# Revit family: PRD_AR_WtrSpplFttngsFrWshBsnsAndTrghs_BasicInstallationKitForTap_F3BX1001,F5BX1001
name_source: partatom
category: Plumbing Fixtures
revit_build: Autodesk Revit 2018 (Build: 20190510_1515(x64)
units: mm (PartAtom-declared; Revit-internal decimal feet)

## family parameters
Cut with Voids When Loaded = Yes
Host = Face
OmniClass Number = 23.45.05.14.99
OmniClass Title = Other Sanitary Washing Plumbing Fixtures
Part Type = Normal
Room Calculation Point = No
Round Connector Dimension = Use Diameter
Shared = No

## types (2) — shared parameters
Application = washing
AssetType = Fixed
BarrierFree = no
Category = Pr_40_20_87_96, Washbasin manual water supply sets
CloseOffRating = 0.0 Pa
Default Elevation = 850 mm  [stored 2.78871 ft]
DiameterNominal = 15.000 mm
DurationUnit = year
Features = For connection to hot and cold water, 174 x 225 mm
Finish = synthetic
FlowCoefficient = 0
FlowColdWater = 0.0 L/s
FlowHotWater = 0.0 L/s
IfcExportAs = IfcValveType
IfcExportType = MIXING
Manufacturer = KWC Group AG
ManufacturerName = KWC Group AG
ManufacturerURL = www.kwc.com
Material = Plastic
MaterialsBody = Brass
MixerControl = Other
NBSDescription = Water supply fittings for wash basins and troughs
NBSReference = 45-35-70/371
OutletConnectionSize = 20 mm  [stored 0.0656168 ft]
PositionOfPowerConnection = from top
ProductInformation = https://pim.kwc.com
Size = 174 x 225
TestPressure = 0.0 Pa
TypeOfMixing = with thermostat / mixer
TypeOfMounting = in-wall installation with box
URL = www.kwc.com
Uniclass2015Code = Pr_40_20_87_96
Uniclass2015Title = Washbasin manual water supply sets
Uniclass2015Version = Products v1.10
ValveMaterial = PRD_AR_PlasticRed
ValveMechanism = Other
ValveOperation = Other
ValvePattern = STRAIGHT_3_PORT
Version = 1
WarrantyDurationUnit = year
zero-valued in all types: NominalHeight, NominalLength, NominalWidth

## per-type parameters (varying)
| type | BIMObjectName | Description | GrossWeight | Model | ModelNumber | ModelReference | Name | NetWeight | Type |
| F3BX1001 | PRD_AR_WaterSupplyFittingsForWashBasinsAndTroughs_BasicInstallationKitForTap_F3BX1001 | R3 basic installation kit for in-wall mounting of finished installation kits DN 15 with mixing unit, for sanitary facilities. For connection to hot and cold water. KWC system box made of plastic, 174 x 225 mm, with connection screws, shell protection, flush connector for flushing, and leak test. | 1.10 kg | F3BX1001 | 2030040479 | F3BX1001 | F3 basic installation kit for tap F3BX1001 | 1.00 kg | for built-in with box |
| F5BX1001 with sliding adhesive flange | PRD_AR_WaterSupplyFittingsForWashBasinsAndTroughs_BasicInstallationKitForTap_F5BX1001 | R5 basic installation kit with sliding adhesive flange for in-wall mounting of finished installation kits DN 15 with mixing unit, for sanitary facilities. For connection to hot and cold water. KWC system box made of plastic, 174 x 225 mm, with lockable connection screws, shell protection, flush connector for flushing, and leak test. Continuously-adjustable sliding adhesive flange with form-closed, flexible, 70 mm wide sealing collar. Sealing collar made of water-tight, permanently-elastic, alkali-resistant, and crack-bridging thermoplastic elastomer with polypropylene fleece for connecting to compound seals in dry and wet construction. | 1.45 kg | F5BX1001 | 2030028992 | F5BX1001 | F5 basic installation kit for tap F5BX1001 | 1.36 kg | for built-in with box and adhesive flange |

note: [stored X ft] marks values corroborated as IEEE doubles in the binary element streams (Revit-internal decimal feet)

## geometry (parser evidence)
native form markers: Sweep x2
no freeform markers — native parametric forms only
